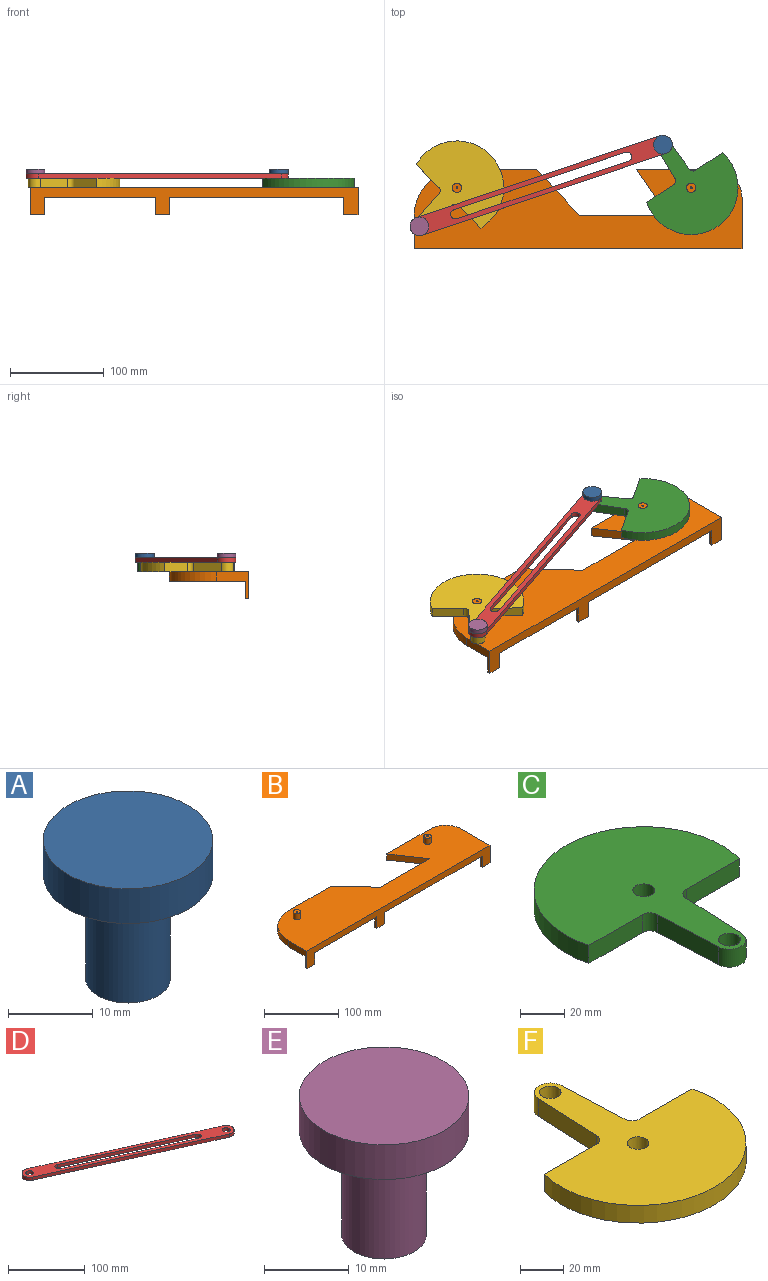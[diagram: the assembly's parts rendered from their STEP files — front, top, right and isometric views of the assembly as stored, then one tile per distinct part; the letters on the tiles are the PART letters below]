
ASSEMBLY  parts=6 mates=6
PART A: 5 faces, bbox 20x20x20 mm
  f0: plane 10x10mm, normal (0,0,-1), area 78.5mm2, adj f1
  f1: cylinder r=5mm len=15mm, axis (0,0,1), area 471.2mm2, adj f0,f4
  f2: cylinder r=10mm len=20mm, axis (0,0,-1), area 314.2mm2, adj f3,f4
  f3: plane 20x20mm, normal (0,0,1), area 314.2mm2, adj f2
  f4: plane 20x20mm, normal (0,0,-1), area 235.6mm2, adj f1,f2
PART B: 28 faces, bbox 350x84.5x38.9 mm
  f0: plane 350x84.55mm, normal (0,0,-1), area 23800.8mm2, adj f1,f2,f3,f9,f10,f11,f12,f13
  f1: plane 34.55x28.93mm, normal (-1,0,0), area 411.7mm2, adj f0,f2,f4,f14,f16,f25
  f2: plane 350x28.93mm, normal (0,-1,0), area 4351.7mm2, adj f0,f1,f3,f4,f14,f15,f17,f18
  f3: plane 54.55x28.93mm, normal (1,0,0), area 611.7mm2, adj f0,f2,f4,f21,f23,f24
  f4: plane 350x84.55mm, normal (0,0,1), area 23807.5mm2, adj f1,f2,f3,f5,f7,f9,f10,f11
  f5: cylinder r=5mm len=10mm, axis (0,0,-1), area 314.2mm2, adj f4,f6
  f6: plane 10x10mm, normal (0,0,1), area 75.4mm2, adj f5,f27
  f7: cylinder r=5mm len=10mm, axis (0,0,-1), area 314.2mm2, adj f4,f8
  f8: plane 10x10mm, normal (0,0,1), area 75.4mm2, adj f7,f26
  f9: plane 81.12x10mm, normal (0,1,0), area 811.2mm2, adj f0,f4,f10,f25
  f10: plane 48.82x45.06mm, normal (0.73,0.68,0), area 664.3mm2, adj f0,f4,f9,f11
  f11: plane 94.41x10mm, normal (0,1,0), area 944.1mm2, adj f0,f4,f10,f12
  f12: plane 48.82x33.26mm, normal (-0.83,-0.56,0), area 590.7mm2, adj f0,f4,f11,f13
  f13: plane 82.66x10mm, normal (0,1,0), area 826.6mm2, adj f0,f4,f12,f24
  f14: plane 15x3.5mm, normal (0,0,-1), area 52.5mm2, adj f1,f2,f15,f16
  f15: plane 18.93x3.5mm, normal (1,0,0), area 66.2mm2, adj f0,f2,f14,f16
  f16: plane 18.93x15mm, normal (0,1,0), area 283.9mm2, adj f0,f1,f14,f15
  f17: plane 18.93x3.5mm, normal (-1,0,0), area 66.2mm2, adj f0,f2,f18,f20
  f18: plane 15x3.5mm, normal (0,0,-1), area 52.5mm2, adj f2,f17,f19,f20
  f19: plane 18.93x3.5mm, normal (1,0,0), area 66.2mm2, adj f0,f2,f18,f20
  f20: plane 18.93x15mm, normal (0,1,0), area 283.9mm2, adj f0,f17,f18,f19
  f21: plane 15x3.5mm, normal (0,0,-1), area 52.5mm2, adj f2,f3,f22,f23
  f22: plane 18.93x3.5mm, normal (-1,0,0), area 66.2mm2, adj f0,f2,f21,f23
  f23: plane 18.93x15mm, normal (0,1,0), area 283.9mm2, adj f0,f3,f21,f22
  f24: cylinder r=30mm len=30mm, axis (0,0,1), area 471.2mm2, adj f0,f3,f4,f13
  f25: cylinder r=50mm len=50mm, axis (0,0,-1), area 785.4mm2, adj f0,f1,f4,f9
  f26: cylinder r=1mm len=20mm, axis (0,0,1), area 125.7mm2, adj f0,f8
  f27: cylinder r=1mm len=20mm, axis (0,0,1), area 125.7mm2, adj f0,f6
PART C: 12 faces, bbox 100x112.5x10 mm
  f0: cylinder r=5mm len=10mm, axis (0,0,-1), area 76.3mm2, adj f1,f7,f10,f11
  f1: plane 37.57x10mm, normal (-1,-0.05,0), area 376.1mm2, adj f0,f2,f10,f11
  f2: cylinder r=7.5mm len=14.99mm, axis (0,0,-1), area 228.9mm2, adj f1,f3,f10,f11
  f3: plane 37.54x10mm, normal (1,-0.04,0), area 375.8mm2, adj f2,f4,f10,f11
  f4: cylinder r=5mm len=10mm, axis (0,0,-1), area 76.4mm2, adj f3,f5,f10,f11
  f5: plane 34.16x10mm, normal (0,-1,0), area 341.6mm2, adj f4,f6,f10,f11
  f6: cylinder r=50mm len=100mm, axis (0,0,-1), area 1833.8mm2, adj f5,f7,f10,f11
  f7: plane 34.08x10mm, normal (0,-1,0), area 340.8mm2, adj f0,f6,f10,f11
  f8: cylinder r=5mm len=10mm, axis (0,0,-1), area 314.2mm2, adj f10,f11
  f9: cylinder r=5mm len=10mm, axis (0,0,-1), area 314.2mm2, adj f10,f11
  f10: plane 112.5x100mm, normal (0,0,1), area 5862.3mm2, adj f0,f1,f2,f3,f4,f5,f6,f7
  f11: plane 112.5x100mm, normal (0,0,-1), area 5862.3mm2, adj f0,f1,f2,f3,f4,f5,f6,f7
PART D: 12 faces, bbox 270x132.5x5 mm
  f0: cylinder r=5mm len=9.56mm, axis (0,0,-1), area 78.5mm2, adj f1,f7,f10,f11
  f1: plane 176.29x79.33mm, normal (-0.41,-0.91,0), area 966.6mm2, adj f0,f2,f10,f11
  f2: cylinder r=5mm len=9.56mm, axis (0,0,-1), area 78.5mm2, adj f1,f7,f10,f11
  f3: cylinder r=10mm len=19.12mm, axis (0,0,-1), area 157.1mm2, adj f4,f8,f10,f11
  f4: plane 250x112.5mm, normal (-0.41,-0.91,0), area 1370.7mm2, adj f3,f5,f10,f11
  f5: cylinder r=10mm len=19.12mm, axis (0,0,-1), area 157.1mm2, adj f4,f8,f10,f11
  f6: cylinder r=5mm len=10mm, axis (0,0,-1), area 157.1mm2, adj f10,f11
  f7: plane 176.29x79.33mm, normal (0.41,0.91,0), area 966.6mm2, adj f0,f2,f10,f11
  f8: plane 250x112.5mm, normal (0.41,0.91,0), area 1370.7mm2, adj f3,f5,f10,f11
  f9: cylinder r=5mm len=10mm, axis (0,0,-1), area 157.1mm2, adj f10,f11
  f10: plane 270x132.5mm, normal (0,0,1), area 3628.3mm2, adj f0,f1,f2,f3,f4,f5,f6,f7
  f11: plane 270x132.5mm, normal (0,0,-1), area 3628.3mm2, adj f0,f1,f2,f3,f4,f5,f6,f7
PART E: 5 faces, bbox 20x20x20 mm
  f0: plane 10x10mm, normal (0,0,-1), area 78.5mm2, adj f1
  f1: cylinder r=5mm len=15mm, axis (0,0,1), area 471.2mm2, adj f0,f4
  f2: cylinder r=10mm len=20mm, axis (0,0,-1), area 314.2mm2, adj f3,f4
  f3: plane 20x20mm, normal (0,0,1), area 314.2mm2, adj f2
  f4: plane 20x20mm, normal (0,0,-1), area 235.6mm2, adj f1,f2
PART F: 12 faces, bbox 100x115x10 mm
  f0: plane 34.05x10mm, normal (0,1,0), area 340.5mm2, adj f1,f7,f10,f11
  f1: cylinder r=50mm len=100mm, axis (0,0,-1), area 1833.8mm2, adj f0,f2,f10,f11
  f2: plane 34.05x10mm, normal (0,1,0), area 340.5mm2, adj f1,f3,f10,f11
  f3: cylinder r=5mm len=10mm, axis (0,0,-1), area 76.4mm2, adj f2,f4,f10,f11
  f4: plane 40.04x10mm, normal (1,0.04,0), area 400.8mm2, adj f3,f5,f10,f11
  f5: cylinder r=7.5mm len=14.99mm, axis (0,0,-1), area 229.1mm2, adj f4,f6,f10,f11
  f6: plane 40.04x10mm, normal (-1,0.04,0), area 400.8mm2, adj f5,f7,f10,f11
  f7: cylinder r=5mm len=10mm, axis (0,0,-1), area 76.4mm2, adj f0,f6,f10,f11
  f8: cylinder r=5mm len=10mm, axis (0,0,-1), area 314.2mm2, adj f10,f11
  f9: cylinder r=5mm len=10mm, axis (0,0,-1), area 314.2mm2, adj f10,f11
  f10: plane 115x100mm, normal (0,0,1), area 5907.5mm2, adj f0,f1,f2,f3,f4,f5,f6,f7
  f11: plane 115x100mm, normal (0,0,-1), area 5907.5mm2, adj f0,f1,f2,f3,f4,f5,f6,f7
PLACE A rot(axis=(0,0,1),123.3deg) t=(436.33,-130.78,0)mm
PLACE B at identity fixed
PLACE C rot(axis=(0,0,-1),146.7deg) t=(507.36,281.7,0)mm
PLACE D rot(axis=(0,0,1),42.8deg) t=(55.25,-97.22,0)mm
PLACE E rot(axis=(0,0,1),45.8deg) t=(61.52,-94.46,0)mm
PLACE F rot(axis=(0,0,1),135.8deg) t=(123.95,79.63,0)mm
MATE revolute C.f6 <-> B.f7  axis (0,0,-1) through (295.79,65,10)mm
MATE revolute D.f3 <-> E.f1  axis (0,0,1) through (5.69,23.8,25)mm
MATE revolute F.f1 <-> B.f5  axis (0,0,-1) through (45.79,65,10)mm
MATE fastened E.f1 <-> F.f5  axis (0,0,-1) through (5.69,23.8,10)mm
MATE fastened A.f1 <-> C.f2  axis (0,0,-1) through (265.6,110.97,10)mm
MATE revolute D.f5 <-> A.f1  axis (0,0,1) through (265.6,110.97,25)mm
